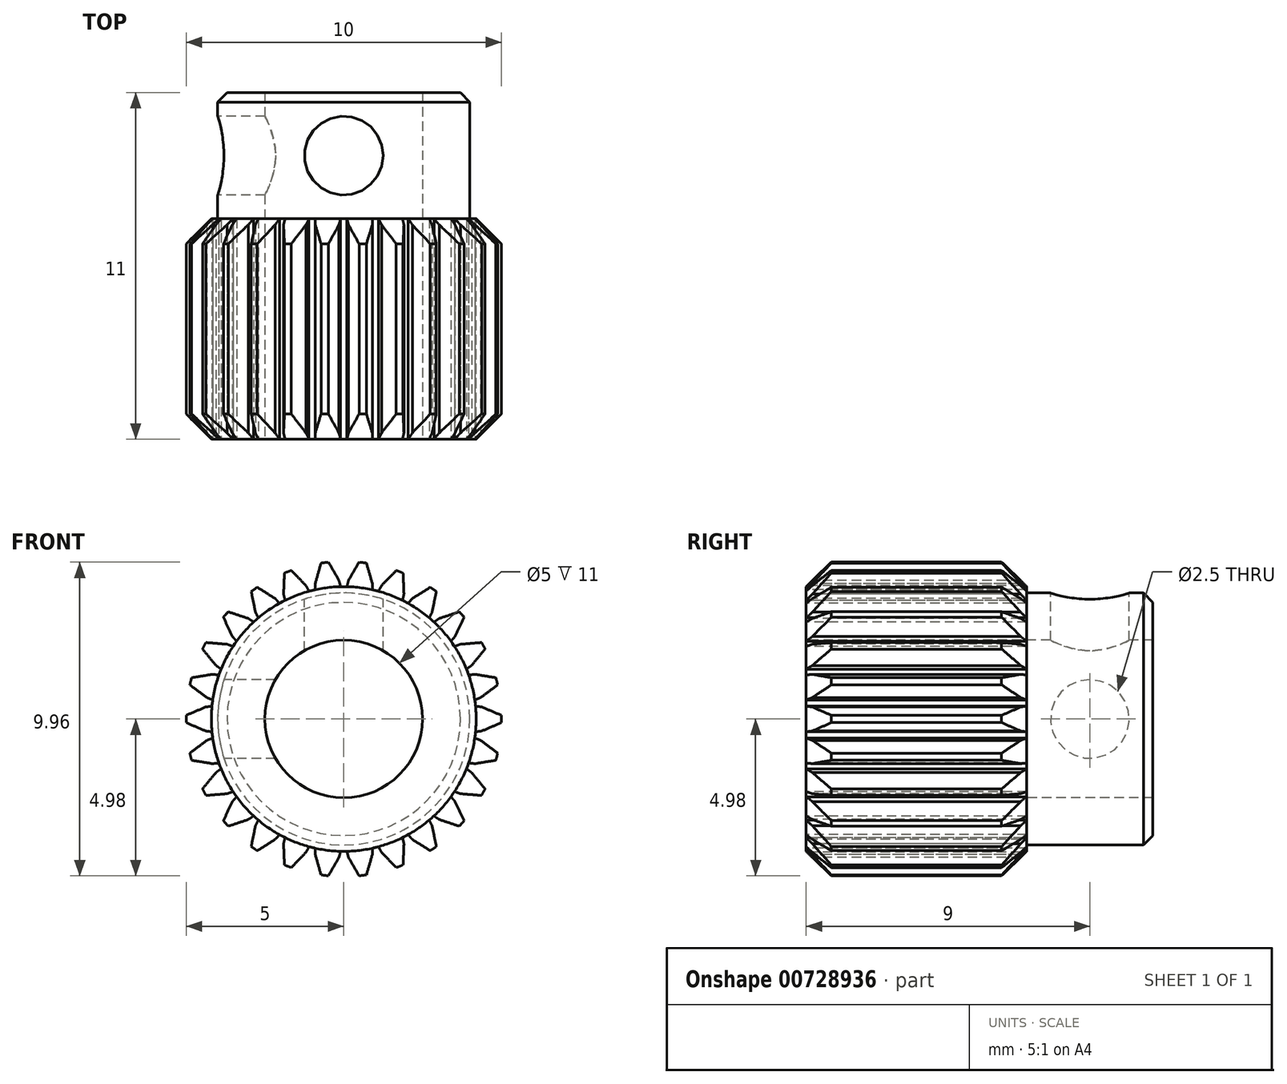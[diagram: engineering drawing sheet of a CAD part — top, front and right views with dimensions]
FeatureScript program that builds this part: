
annotation { "Feature Type Name" : "Feature", "Feature Type Description" : "" }
export const myFeature = defineFeature(function(context is Context, id is Id, definition is map)
    precondition{}
    {
        {
            var Q0;
            Q0=qCreatedBy(makeId("Right.planeOp"),FACE);
            var sketch = newSketch(context, id + "F0", { "sketchPlane" : qUnion([Q0])});
            skLineSegment(sketch, "E0", {"start": v(-5.5, 0) * mm, "end": v(5.5, 0) * mm, "construction": true});
            skLineSegment(sketch, "E1", {"start": v(-5.5, 2.5) * mm, "end": v(5.5, 2.5) * mm});
            skLineSegment(sketch, "E2", {"start": v(5.5, 2.5) * mm, "end": v(5.5, 4) * mm});
            skLineSegment(sketch, "E3", {"start": v(5.5, 4) * mm, "end": v(1.5, 4) * mm});
            skLineSegment(sketch, "E4", {"start": v(1.5, 4) * mm, "end": v(1.5, 5) * mm});
            skLineSegment(sketch, "E5", {"start": v(1.5, 5) * mm, "end": v(-5.5, 5) * mm});
            skLineSegment(sketch, "E6", {"start": v(-5.5, 5) * mm, "end": v(-5.5, 2.5) * mm});
            skSolve(sketch);
        }
        {
            var Q0;
            Q0=makeQuery(id+"F0.imprint","IMPRINT",FACE,{"disambiguationData":[TD([[makeQuery(id+"F0.imprint","IMPRINT",EDGE,{"derivedFrom":sQuery(id+"F0.wireOp",EDGE,"E1")}),1.0]])]});
            var Q1;
            Q1=sQuery(id+"F0.wireOp",EDGE,"E0");
            revolve(context, id + "F1", {"entities" : qUnion([Q0]), "axis" : qUnion([Q1]), "revolveType" : RevolveType.FULL});
        }
        {
            var Q0;
            Q0=makeQuery(id+"F1.opRevolve","SWEPT_EDGE",EDGE,{"disambiguationData":[OSD([sQuery(id+"F0.wireOp",EDGE,"E4"),sQuery(id+"F0.wireOp",EDGE,"E5")])]});
            var Q1;
            Q1=makeQuery(id+"F1.opRevolve","SWEPT_EDGE",EDGE,{"disambiguationData":[OSD([sQuery(id+"F0.wireOp",EDGE,"E5"),sQuery(id+"F0.wireOp",EDGE,"E6")])]});
            chamfer(context, id + "F2", {"entities" : qUnion([Q0, Q1]), "width" : .8 * mm, "tangentPropagation" : true});
        }
        {
            var Q0;
            Q0=makeQuery(id+"F1.opRevolve","SWEPT_FACE",FACE,{"disambiguationData":[OSD([sQuery(id+"F0.wireOp",EDGE,"E6")])]});
            var sketch = newSketch(context, id + "F3", { "sketchPlane" : qUnion([Q0])});
            skLineSegment(sketch, "E7", {"start": v(0, 0) * mm, "end": v(0, 5) * mm, "construction": true});
            skLineSegment(sketch, "E8", {"start": v(0, 4.2) * mm, "end": v(-0.1, 4.2) * mm});
            skLineSegment(sketch, "E9", {"start": v(-0.1, 4.2) * mm, "end": v(-0.15, 4.4) * mm});
            skLineSegment(sketch, "E10", {"start": v(-0.15, 4.4) * mm, "end": v(-0.5, 5) * mm});
            skLineSegment(sketch, "E11", {"start": v(0, 5) * mm, "end": v(-0.5, 5) * mm});
            skLineSegment(sketch, "E12.MirrorCS", {"start": v(0, 5) * mm, "end": v(0.5, 5) * mm});
            skLineSegment(sketch, "E13.MirrorCS", {"start": v(0.15, 4.4) * mm, "end": v(0.5, 5) * mm});
            skLineSegment(sketch, "E14.MirrorCS", {"start": v(0, 4.2) * mm, "end": v(0.1, 4.2) * mm});
            skLineSegment(sketch, "E15.MirrorCS", {"start": v(0.1, 4.2) * mm, "end": v(0.15, 4.4) * mm});
            skLineSegment(sketch, "E16.1.0", {"start": v(-0.9, 4.3) * mm, "end": v(-0.71, 4.97) * mm});
            skLineSegment(sketch, "E16.1.1", {"start": v(-1.2, 4.85) * mm, "end": v(-0.71, 4.97) * mm});
            skLineSegment(sketch, "E16.1.2", {"start": v(-1.2, 4.85) * mm, "end": v(-1.68, 4.74) * mm});
            skLineSegment(sketch, "E16.1.3", {"start": v(-1.2, 4.23) * mm, "end": v(-1.68, 4.74) * mm});
            skLineSegment(sketch, "E16.1.4", {"start": v(-1.1, 4.05) * mm, "end": v(-1.2, 4.23) * mm});
            skLineSegment(sketch, "E16.1.5", {"start": v(-0.9, 4.1) * mm, "end": v(-0.9, 4.3) * mm});
            skLineSegment(sketch, "E16.1.6", {"start": v(-1, 4.08) * mm, "end": v(-1.1, 4.05) * mm});
            skLineSegment(sketch, "E16.1.7", {"start": v(-1, 4.08) * mm, "end": v(-0.9, 4.1) * mm});
            skLineSegment(sketch, "E16.2.0", {"start": v(-1.9, 3.96) * mm, "end": v(-1.88, 4.66) * mm});
            skLineSegment(sketch, "E16.2.1", {"start": v(-2.32, 4.43) * mm, "end": v(-1.88, 4.66) * mm});
            skLineSegment(sketch, "E16.2.2", {"start": v(-2.32, 4.43) * mm, "end": v(-2.77, 4.2) * mm});
            skLineSegment(sketch, "E16.2.3", {"start": v(-2.17, 3.82) * mm, "end": v(-2.77, 4.2) * mm});
            skLineSegment(sketch, "E16.2.4", {"start": v(-2.04, 3.67) * mm, "end": v(-2.17, 3.82) * mm});
            skLineSegment(sketch, "E16.2.5", {"start": v(-1.86, 3.77) * mm, "end": v(-1.9, 3.96) * mm});
            skLineSegment(sketch, "E16.2.6", {"start": v(-1.95, 3.72) * mm, "end": v(-2.04, 3.67) * mm});
            skLineSegment(sketch, "E16.2.7", {"start": v(-1.95, 3.72) * mm, "end": v(-1.86, 3.77) * mm});
            skLineSegment(sketch, "E16.3.0", {"start": v(-2.8, 3.39) * mm, "end": v(-2.94, 4.07) * mm});
            skLineSegment(sketch, "E16.3.1", {"start": v(-3.32, 3.74) * mm, "end": v(-2.94, 4.07) * mm});
            skLineSegment(sketch, "E16.3.2", {"start": v(-3.32, 3.74) * mm, "end": v(-3.69, 3.41) * mm});
            skLineSegment(sketch, "E16.3.3", {"start": v(-3.03, 3.19) * mm, "end": v(-3.69, 3.41) * mm});
            skLineSegment(sketch, "E16.3.4", {"start": v(-2.86, 3.08) * mm, "end": v(-3.03, 3.19) * mm});
            skLineSegment(sketch, "E16.3.5", {"start": v(-2.71, 3.21) * mm, "end": v(-2.8, 3.39) * mm});
            skLineSegment(sketch, "E16.3.6", {"start": v(-2.79, 3.14) * mm, "end": v(-2.86, 3.08) * mm});
            skLineSegment(sketch, "E16.3.7", {"start": v(-2.79, 3.14) * mm, "end": v(-2.71, 3.21) * mm});
            skLineSegment(sketch, "E16.4.0", {"start": v(-3.53, 2.62) * mm, "end": v(-3.83, 3.25) * mm});
            skLineSegment(sketch, "E16.4.1", {"start": v(-4.11, 2.84) * mm, "end": v(-3.83, 3.25) * mm});
            skLineSegment(sketch, "E16.4.2", {"start": v(-4.11, 2.84) * mm, "end": v(-4.4, 2.43) * mm});
            skLineSegment(sketch, "E16.4.3", {"start": v(-3.7, 2.37) * mm, "end": v(-4.4, 2.43) * mm});
            skLineSegment(sketch, "E16.4.4", {"start": v(-3.51, 2.3) * mm, "end": v(-3.7, 2.37) * mm});
            skLineSegment(sketch, "E16.4.5", {"start": v(-3.4, 2.47) * mm, "end": v(-3.53, 2.62) * mm});
            skLineSegment(sketch, "E16.4.6", {"start": v(-3.46, 2.39) * mm, "end": v(-3.51, 2.3) * mm});
            skLineSegment(sketch, "E16.4.7", {"start": v(-3.46, 2.39) * mm, "end": v(-3.4, 2.47) * mm});
            skLineSegment(sketch, "E16.5.0", {"start": v(-4.06, 1.7) * mm, "end": v(-4.5, 2.24) * mm});
            skLineSegment(sketch, "E16.5.1", {"start": v(-4.68, 1.77) * mm, "end": v(-4.5, 2.24) * mm});
            skLineSegment(sketch, "E16.5.2", {"start": v(-4.68, 1.77) * mm, "end": v(-4.85, 1.3) * mm});
            skLineSegment(sketch, "E16.5.3", {"start": v(-4.16, 1.42) * mm, "end": v(-4.85, 1.3) * mm});
            skLineSegment(sketch, "E16.5.4", {"start": v(-3.96, 1.4) * mm, "end": v(-4.16, 1.42) * mm});
            skLineSegment(sketch, "E16.5.5", {"start": v(-3.9, 1.58) * mm, "end": v(-4.06, 1.7) * mm});
            skLineSegment(sketch, "E16.5.6", {"start": v(-3.93, 1.49) * mm, "end": v(-3.96, 1.4) * mm});
            skLineSegment(sketch, "E16.5.7", {"start": v(-3.93, 1.49) * mm, "end": v(-3.9, 1.58) * mm});
            skLineSegment(sketch, "E16.6.0", {"start": v(-4.34, 0.68) * mm, "end": v(-4.9, 1.1) * mm});
            skLineSegment(sketch, "E16.6.1", {"start": v(-4.96, 0.6) * mm, "end": v(-4.9, 1.1) * mm});
            skLineSegment(sketch, "E16.6.2", {"start": v(-4.96, 0.6) * mm, "end": v(-5.02, 0.1) * mm});
            skLineSegment(sketch, "E16.6.3", {"start": v(-4.38, 0.38) * mm, "end": v(-5.02, 0.1) * mm});
            skLineSegment(sketch, "E16.6.4", {"start": v(-4.18, 0.4) * mm, "end": v(-4.38, 0.38) * mm});
            skLineSegment(sketch, "E16.6.5", {"start": v(-4.16, 0.6) * mm, "end": v(-4.34, 0.68) * mm});
            skLineSegment(sketch, "E16.6.6", {"start": v(-4.17, 0.5) * mm, "end": v(-4.18, 0.4) * mm});
            skLineSegment(sketch, "E16.6.7", {"start": v(-4.17, 0.5) * mm, "end": v(-4.16, 0.6) * mm});
            skLineSegment(sketch, "E16.7.0", {"start": v(-4.38, -0.38) * mm, "end": v(-5.02, -0.1) * mm});
            skLineSegment(sketch, "E16.7.1", {"start": v(-4.96, -0.6) * mm, "end": v(-5.02, -0.1) * mm});
            skLineSegment(sketch, "E16.7.2", {"start": v(-4.96, -0.6) * mm, "end": v(-4.9, -1.1) * mm});
            skLineSegment(sketch, "E16.7.3", {"start": v(-4.34, -0.68) * mm, "end": v(-4.9, -1.1) * mm});
            skLineSegment(sketch, "E16.7.4", {"start": v(-4.16, -0.6) * mm, "end": v(-4.34, -0.68) * mm});
            skLineSegment(sketch, "E16.7.5", {"start": v(-4.18, -0.4) * mm, "end": v(-4.38, -0.38) * mm});
            skLineSegment(sketch, "E16.7.6", {"start": v(-4.17, -0.5) * mm, "end": v(-4.16, -0.6) * mm});
            skLineSegment(sketch, "E16.7.7", {"start": v(-4.17, -0.5) * mm, "end": v(-4.18, -0.4) * mm});
            skLineSegment(sketch, "E16.8.0", {"start": v(-4.16, -1.42) * mm, "end": v(-4.85, -1.3) * mm});
            skLineSegment(sketch, "E16.8.1", {"start": v(-4.68, -1.77) * mm, "end": v(-4.85, -1.3) * mm});
            skLineSegment(sketch, "E16.8.2", {"start": v(-4.68, -1.77) * mm, "end": v(-4.5, -2.24) * mm});
            skLineSegment(sketch, "E16.8.3", {"start": v(-4.06, -1.7) * mm, "end": v(-4.5, -2.24) * mm});
            skLineSegment(sketch, "E16.8.4", {"start": v(-3.9, -1.58) * mm, "end": v(-4.06, -1.7) * mm});
            skLineSegment(sketch, "E16.8.5", {"start": v(-3.96, -1.4) * mm, "end": v(-4.16, -1.42) * mm});
            skLineSegment(sketch, "E16.8.6", {"start": v(-3.93, -1.49) * mm, "end": v(-3.9, -1.58) * mm});
            skLineSegment(sketch, "E16.8.7", {"start": v(-3.93, -1.49) * mm, "end": v(-3.96, -1.4) * mm});
            skLineSegment(sketch, "E16.9.0", {"start": v(-3.7, -2.37) * mm, "end": v(-4.4, -2.43) * mm});
            skLineSegment(sketch, "E16.9.1", {"start": v(-4.11, -2.84) * mm, "end": v(-4.4, -2.43) * mm});
            skLineSegment(sketch, "E16.9.2", {"start": v(-4.11, -2.84) * mm, "end": v(-3.83, -3.25) * mm});
            skLineSegment(sketch, "E16.9.3", {"start": v(-3.53, -2.62) * mm, "end": v(-3.83, -3.25) * mm});
            skLineSegment(sketch, "E16.9.4", {"start": v(-3.4, -2.47) * mm, "end": v(-3.53, -2.62) * mm});
            skLineSegment(sketch, "E16.9.5", {"start": v(-3.51, -2.3) * mm, "end": v(-3.7, -2.37) * mm});
            skLineSegment(sketch, "E16.9.6", {"start": v(-3.46, -2.39) * mm, "end": v(-3.4, -2.47) * mm});
            skLineSegment(sketch, "E16.9.7", {"start": v(-3.46, -2.39) * mm, "end": v(-3.51, -2.3) * mm});
            skLineSegment(sketch, "E16.10.0", {"start": v(-3.03, -3.19) * mm, "end": v(-3.69, -3.41) * mm});
            skLineSegment(sketch, "E16.10.1", {"start": v(-3.32, -3.74) * mm, "end": v(-3.69, -3.41) * mm});
            skLineSegment(sketch, "E16.10.2", {"start": v(-3.32, -3.74) * mm, "end": v(-2.94, -4.07) * mm});
            skLineSegment(sketch, "E16.10.3", {"start": v(-2.8, -3.39) * mm, "end": v(-2.94, -4.07) * mm});
            skLineSegment(sketch, "E16.10.4", {"start": v(-2.71, -3.21) * mm, "end": v(-2.8, -3.39) * mm});
            skLineSegment(sketch, "E16.10.5", {"start": v(-2.86, -3.08) * mm, "end": v(-3.03, -3.19) * mm});
            skLineSegment(sketch, "E16.10.6", {"start": v(-2.79, -3.14) * mm, "end": v(-2.71, -3.21) * mm});
            skLineSegment(sketch, "E16.10.7", {"start": v(-2.79, -3.14) * mm, "end": v(-2.86, -3.08) * mm});
            skLineSegment(sketch, "E16.11.0", {"start": v(-2.17, -3.82) * mm, "end": v(-2.77, -4.2) * mm});
            skLineSegment(sketch, "E16.11.1", {"start": v(-2.32, -4.43) * mm, "end": v(-2.77, -4.2) * mm});
            skLineSegment(sketch, "E16.11.2", {"start": v(-2.32, -4.43) * mm, "end": v(-1.88, -4.66) * mm});
            skLineSegment(sketch, "E16.11.3", {"start": v(-1.9, -3.96) * mm, "end": v(-1.88, -4.66) * mm});
            skLineSegment(sketch, "E16.11.4", {"start": v(-1.86, -3.77) * mm, "end": v(-1.9, -3.96) * mm});
            skLineSegment(sketch, "E16.11.5", {"start": v(-2.04, -3.67) * mm, "end": v(-2.17, -3.82) * mm});
            skLineSegment(sketch, "E16.11.6", {"start": v(-1.95, -3.72) * mm, "end": v(-1.86, -3.77) * mm});
            skLineSegment(sketch, "E16.11.7", {"start": v(-1.95, -3.72) * mm, "end": v(-2.04, -3.67) * mm});
            skLineSegment(sketch, "E16.12.0", {"start": v(-1.2, -4.23) * mm, "end": v(-1.68, -4.74) * mm});
            skLineSegment(sketch, "E16.12.1", {"start": v(-1.2, -4.85) * mm, "end": v(-1.68, -4.74) * mm});
            skLineSegment(sketch, "E16.12.2", {"start": v(-1.2, -4.85) * mm, "end": v(-0.71, -4.97) * mm});
            skLineSegment(sketch, "E16.12.3", {"start": v(-0.9, -4.3) * mm, "end": v(-0.71, -4.97) * mm});
            skLineSegment(sketch, "E16.12.4", {"start": v(-0.9, -4.1) * mm, "end": v(-0.9, -4.3) * mm});
            skLineSegment(sketch, "E16.12.5", {"start": v(-1.1, -4.05) * mm, "end": v(-1.2, -4.23) * mm});
            skLineSegment(sketch, "E16.12.6", {"start": v(-1, -4.08) * mm, "end": v(-0.9, -4.1) * mm});
            skLineSegment(sketch, "E16.12.7", {"start": v(-1, -4.08) * mm, "end": v(-1.1, -4.05) * mm});
            skLineSegment(sketch, "E16.13.0", {"start": v(-0.15, -4.4) * mm, "end": v(-0.5, -5) * mm});
            skLineSegment(sketch, "E16.13.1", {"start": v(0, -5) * mm, "end": v(-0.5, -5) * mm});
            skLineSegment(sketch, "E16.13.2", {"start": v(0, -5) * mm, "end": v(0.5, -5) * mm});
            skLineSegment(sketch, "E16.13.3", {"start": v(0.15, -4.4) * mm, "end": v(0.5, -5) * mm});
            skLineSegment(sketch, "E16.13.4", {"start": v(0.1, -4.2) * mm, "end": v(0.15, -4.4) * mm});
            skLineSegment(sketch, "E16.13.5", {"start": v(-0.1, -4.2) * mm, "end": v(-0.15, -4.4) * mm});
            skLineSegment(sketch, "E16.13.6", {"start": v(0, -4.2) * mm, "end": v(0.1, -4.2) * mm});
            skLineSegment(sketch, "E16.13.7", {"start": v(0, -4.2) * mm, "end": v(-0.1, -4.2) * mm});
            skLineSegment(sketch, "E16.14.0", {"start": v(0.9, -4.3) * mm, "end": v(0.71, -4.97) * mm});
            skLineSegment(sketch, "E16.14.1", {"start": v(1.2, -4.85) * mm, "end": v(0.71, -4.97) * mm});
            skLineSegment(sketch, "E16.14.2", {"start": v(1.2, -4.85) * mm, "end": v(1.68, -4.74) * mm});
            skLineSegment(sketch, "E16.14.3", {"start": v(1.2, -4.23) * mm, "end": v(1.68, -4.74) * mm});
            skLineSegment(sketch, "E16.14.4", {"start": v(1.1, -4.05) * mm, "end": v(1.2, -4.23) * mm});
            skLineSegment(sketch, "E16.14.5", {"start": v(0.9, -4.1) * mm, "end": v(0.9, -4.3) * mm});
            skLineSegment(sketch, "E16.14.6", {"start": v(1, -4.08) * mm, "end": v(1.1, -4.05) * mm});
            skLineSegment(sketch, "E16.14.7", {"start": v(1, -4.08) * mm, "end": v(0.9, -4.1) * mm});
            skLineSegment(sketch, "E16.15.0", {"start": v(1.9, -3.96) * mm, "end": v(1.88, -4.66) * mm});
            skLineSegment(sketch, "E16.15.1", {"start": v(2.32, -4.43) * mm, "end": v(1.88, -4.66) * mm});
            skLineSegment(sketch, "E16.15.2", {"start": v(2.32, -4.43) * mm, "end": v(2.77, -4.2) * mm});
            skLineSegment(sketch, "E16.15.3", {"start": v(2.17, -3.82) * mm, "end": v(2.77, -4.2) * mm});
            skLineSegment(sketch, "E16.15.4", {"start": v(2.04, -3.67) * mm, "end": v(2.17, -3.82) * mm});
            skLineSegment(sketch, "E16.15.5", {"start": v(1.86, -3.77) * mm, "end": v(1.9, -3.96) * mm});
            skLineSegment(sketch, "E16.15.6", {"start": v(1.95, -3.72) * mm, "end": v(2.04, -3.67) * mm});
            skLineSegment(sketch, "E16.15.7", {"start": v(1.95, -3.72) * mm, "end": v(1.86, -3.77) * mm});
            skLineSegment(sketch, "E16.16.0", {"start": v(2.8, -3.39) * mm, "end": v(2.94, -4.07) * mm});
            skLineSegment(sketch, "E16.16.1", {"start": v(3.32, -3.74) * mm, "end": v(2.94, -4.07) * mm});
            skLineSegment(sketch, "E16.16.2", {"start": v(3.32, -3.74) * mm, "end": v(3.69, -3.41) * mm});
            skLineSegment(sketch, "E16.16.3", {"start": v(3.03, -3.19) * mm, "end": v(3.69, -3.41) * mm});
            skLineSegment(sketch, "E16.16.4", {"start": v(2.86, -3.08) * mm, "end": v(3.03, -3.19) * mm});
            skLineSegment(sketch, "E16.16.5", {"start": v(2.71, -3.21) * mm, "end": v(2.8, -3.39) * mm});
            skLineSegment(sketch, "E16.16.6", {"start": v(2.79, -3.14) * mm, "end": v(2.86, -3.08) * mm});
            skLineSegment(sketch, "E16.16.7", {"start": v(2.79, -3.14) * mm, "end": v(2.71, -3.21) * mm});
            skLineSegment(sketch, "E16.17.0", {"start": v(3.53, -2.62) * mm, "end": v(3.83, -3.25) * mm});
            skLineSegment(sketch, "E16.17.1", {"start": v(4.11, -2.84) * mm, "end": v(3.83, -3.25) * mm});
            skLineSegment(sketch, "E16.17.2", {"start": v(4.11, -2.84) * mm, "end": v(4.4, -2.43) * mm});
            skLineSegment(sketch, "E16.17.3", {"start": v(3.7, -2.37) * mm, "end": v(4.4, -2.43) * mm});
            skLineSegment(sketch, "E16.17.4", {"start": v(3.51, -2.3) * mm, "end": v(3.7, -2.37) * mm});
            skLineSegment(sketch, "E16.17.5", {"start": v(3.4, -2.47) * mm, "end": v(3.53, -2.62) * mm});
            skLineSegment(sketch, "E16.17.6", {"start": v(3.46, -2.39) * mm, "end": v(3.51, -2.3) * mm});
            skLineSegment(sketch, "E16.17.7", {"start": v(3.46, -2.39) * mm, "end": v(3.4, -2.47) * mm});
            skLineSegment(sketch, "E16.18.0", {"start": v(4.06, -1.7) * mm, "end": v(4.5, -2.24) * mm});
            skLineSegment(sketch, "E16.18.1", {"start": v(4.68, -1.77) * mm, "end": v(4.5, -2.24) * mm});
            skLineSegment(sketch, "E16.18.2", {"start": v(4.68, -1.77) * mm, "end": v(4.85, -1.3) * mm});
            skLineSegment(sketch, "E16.18.3", {"start": v(4.16, -1.42) * mm, "end": v(4.85, -1.3) * mm});
            skLineSegment(sketch, "E16.18.4", {"start": v(3.96, -1.4) * mm, "end": v(4.16, -1.42) * mm});
            skLineSegment(sketch, "E16.18.5", {"start": v(3.9, -1.58) * mm, "end": v(4.06, -1.7) * mm});
            skLineSegment(sketch, "E16.18.6", {"start": v(3.93, -1.49) * mm, "end": v(3.96, -1.4) * mm});
            skLineSegment(sketch, "E16.18.7", {"start": v(3.93, -1.49) * mm, "end": v(3.9, -1.58) * mm});
            skLineSegment(sketch, "E16.19.0", {"start": v(4.34, -0.68) * mm, "end": v(4.9, -1.1) * mm});
            skLineSegment(sketch, "E16.19.1", {"start": v(4.96, -0.6) * mm, "end": v(4.9, -1.1) * mm});
            skLineSegment(sketch, "E16.19.2", {"start": v(4.96, -0.6) * mm, "end": v(5.02, -0.1) * mm});
            skLineSegment(sketch, "E16.19.3", {"start": v(4.38, -0.38) * mm, "end": v(5.02, -0.1) * mm});
            skLineSegment(sketch, "E16.19.4", {"start": v(4.18, -0.4) * mm, "end": v(4.38, -0.38) * mm});
            skLineSegment(sketch, "E16.19.5", {"start": v(4.16, -0.6) * mm, "end": v(4.34, -0.68) * mm});
            skLineSegment(sketch, "E16.19.6", {"start": v(4.17, -0.5) * mm, "end": v(4.18, -0.4) * mm});
            skLineSegment(sketch, "E16.19.7", {"start": v(4.17, -0.5) * mm, "end": v(4.16, -0.6) * mm});
            skLineSegment(sketch, "E16.20.0", {"start": v(4.38, 0.38) * mm, "end": v(5.02, 0.1) * mm});
            skLineSegment(sketch, "E16.20.1", {"start": v(4.96, 0.6) * mm, "end": v(5.02, 0.1) * mm});
            skLineSegment(sketch, "E16.20.2", {"start": v(4.96, 0.6) * mm, "end": v(4.9, 1.1) * mm});
            skLineSegment(sketch, "E16.20.3", {"start": v(4.34, 0.68) * mm, "end": v(4.9, 1.1) * mm});
            skLineSegment(sketch, "E16.20.4", {"start": v(4.16, 0.6) * mm, "end": v(4.34, 0.68) * mm});
            skLineSegment(sketch, "E16.20.5", {"start": v(4.18, 0.4) * mm, "end": v(4.38, 0.38) * mm});
            skLineSegment(sketch, "E16.20.6", {"start": v(4.17, 0.5) * mm, "end": v(4.16, 0.6) * mm});
            skLineSegment(sketch, "E16.20.7", {"start": v(4.17, 0.5) * mm, "end": v(4.18, 0.4) * mm});
            skLineSegment(sketch, "E16.21.0", {"start": v(4.16, 1.42) * mm, "end": v(4.85, 1.3) * mm});
            skLineSegment(sketch, "E16.21.1", {"start": v(4.68, 1.77) * mm, "end": v(4.85, 1.3) * mm});
            skLineSegment(sketch, "E16.21.2", {"start": v(4.68, 1.77) * mm, "end": v(4.5, 2.24) * mm});
            skLineSegment(sketch, "E16.21.3", {"start": v(4.06, 1.7) * mm, "end": v(4.5, 2.24) * mm});
            skLineSegment(sketch, "E16.21.4", {"start": v(3.9, 1.58) * mm, "end": v(4.06, 1.7) * mm});
            skLineSegment(sketch, "E16.21.5", {"start": v(3.96, 1.4) * mm, "end": v(4.16, 1.42) * mm});
            skLineSegment(sketch, "E16.21.6", {"start": v(3.93, 1.49) * mm, "end": v(3.9, 1.58) * mm});
            skLineSegment(sketch, "E16.21.7", {"start": v(3.93, 1.49) * mm, "end": v(3.96, 1.4) * mm});
            skLineSegment(sketch, "E16.22.0", {"start": v(3.7, 2.37) * mm, "end": v(4.4, 2.43) * mm});
            skLineSegment(sketch, "E16.22.1", {"start": v(4.11, 2.84) * mm, "end": v(4.4, 2.43) * mm});
            skLineSegment(sketch, "E16.22.2", {"start": v(4.11, 2.84) * mm, "end": v(3.83, 3.25) * mm});
            skLineSegment(sketch, "E16.22.3", {"start": v(3.53, 2.62) * mm, "end": v(3.83, 3.25) * mm});
            skLineSegment(sketch, "E16.22.4", {"start": v(3.4, 2.47) * mm, "end": v(3.53, 2.62) * mm});
            skLineSegment(sketch, "E16.22.5", {"start": v(3.51, 2.3) * mm, "end": v(3.7, 2.37) * mm});
            skLineSegment(sketch, "E16.22.6", {"start": v(3.46, 2.39) * mm, "end": v(3.4, 2.47) * mm});
            skLineSegment(sketch, "E16.22.7", {"start": v(3.46, 2.39) * mm, "end": v(3.51, 2.3) * mm});
            skLineSegment(sketch, "E16.23.0", {"start": v(3.03, 3.19) * mm, "end": v(3.69, 3.41) * mm});
            skLineSegment(sketch, "E16.23.1", {"start": v(3.32, 3.74) * mm, "end": v(3.69, 3.41) * mm});
            skLineSegment(sketch, "E16.23.2", {"start": v(3.32, 3.74) * mm, "end": v(2.94, 4.07) * mm});
            skLineSegment(sketch, "E16.23.3", {"start": v(2.8, 3.39) * mm, "end": v(2.94, 4.07) * mm});
            skLineSegment(sketch, "E16.23.4", {"start": v(2.71, 3.21) * mm, "end": v(2.8, 3.39) * mm});
            skLineSegment(sketch, "E16.23.5", {"start": v(2.86, 3.08) * mm, "end": v(3.03, 3.19) * mm});
            skLineSegment(sketch, "E16.23.6", {"start": v(2.79, 3.14) * mm, "end": v(2.71, 3.21) * mm});
            skLineSegment(sketch, "E16.23.7", {"start": v(2.79, 3.14) * mm, "end": v(2.86, 3.08) * mm});
            skLineSegment(sketch, "E16.24.0", {"start": v(2.17, 3.82) * mm, "end": v(2.77, 4.2) * mm});
            skLineSegment(sketch, "E16.24.1", {"start": v(2.32, 4.43) * mm, "end": v(2.77, 4.2) * mm});
            skLineSegment(sketch, "E16.24.2", {"start": v(2.32, 4.43) * mm, "end": v(1.88, 4.66) * mm});
            skLineSegment(sketch, "E16.24.3", {"start": v(1.9, 3.96) * mm, "end": v(1.88, 4.66) * mm});
            skLineSegment(sketch, "E16.24.4", {"start": v(1.86, 3.77) * mm, "end": v(1.9, 3.96) * mm});
            skLineSegment(sketch, "E16.24.5", {"start": v(2.04, 3.67) * mm, "end": v(2.17, 3.82) * mm});
            skLineSegment(sketch, "E16.24.6", {"start": v(1.95, 3.72) * mm, "end": v(1.86, 3.77) * mm});
            skLineSegment(sketch, "E16.24.7", {"start": v(1.95, 3.72) * mm, "end": v(2.04, 3.67) * mm});
            skLineSegment(sketch, "E16.25.0", {"start": v(1.2, 4.23) * mm, "end": v(1.68, 4.74) * mm});
            skLineSegment(sketch, "E16.25.1", {"start": v(1.2, 4.85) * mm, "end": v(1.68, 4.74) * mm});
            skLineSegment(sketch, "E16.25.2", {"start": v(1.2, 4.85) * mm, "end": v(0.71, 4.97) * mm});
            skLineSegment(sketch, "E16.25.3", {"start": v(0.9, 4.3) * mm, "end": v(0.71, 4.97) * mm});
            skLineSegment(sketch, "E16.25.4", {"start": v(0.9, 4.1) * mm, "end": v(0.9, 4.3) * mm});
            skLineSegment(sketch, "E16.25.5", {"start": v(1.1, 4.05) * mm, "end": v(1.2, 4.23) * mm});
            skLineSegment(sketch, "E16.25.6", {"start": v(1, 4.08) * mm, "end": v(0.9, 4.1) * mm});
            skLineSegment(sketch, "E16.25.7", {"start": v(1, 4.08) * mm, "end": v(1.1, 4.05) * mm});
            skPoint(sketch, "E16.center", {"position": v(0, 0) * mm});
            skSolve(sketch);
        }
        {
            var Q0;
            Q0=qSketchRegion(id+"F3",true);
            extrude(context, id + "F4", {"entities" : qUnion([Q0]), "operationType" : NewBodyOperationType.REMOVE, "oppositeDirection" : true, "depth" : 10 * mm});
        }
        {
            var Q0;
            Q0=makeQuery(id+"F1.opRevolve","SWEPT_FACE",FACE,{"disambiguationData":[OSD([sQuery(id+"F0.wireOp",EDGE,"E2")])]});
            cPlane(context, id + "F5", {"entities" : qUnion([Q0]), "cplaneType" : CPlaneType.OFFSET, "offset" : 2 * mm, "oppositeDirection" : true, "width" : 150 * mm, "height" : 150 * mm});
        }
        {
            var Q0;
            Q0=qCreatedBy(id+"F5.planeOp",FACE);
            var sketch = newSketch(context, id + "F6", { "sketchPlane" : qUnion([Q0])});
            skLineSegment(sketch, "E17", {"start": v(0, 4) * mm, "end": v(0, 0) * mm});
            skLineSegment(sketch, "E18", {"start": v(0, 0) * mm, "end": v(4, 0) * mm});
            skSolve(sketch);
        }
        {
            var Q0;
            Q0=sQuery(id+"F6.wireOp",VERTEX,"E17.start");
            var Q1;
            Q1=sQuery(id+"F6.wireOp",EDGE,"E17");
            cPlane(context, id + "F7", {"entities" : qUnion([Q0, Q1]), "cplaneType" : CPlaneType.LINE_POINT, "offset" : 25 * mm, "width" : 150 * mm, "height" : 150 * mm});
        }
        {
            var Q0;
            Q0=qCreatedBy(id+"F7.planeOp",FACE);
            var sketch = newSketch(context, id + "F8", { "sketchPlane" : qUnion([Q0])});
            skPoint(sketch, "E19.0", {"position": v(0, -3.5) * mm});
            skSolve(sketch);
        }
        {
            var Q0;
            Q0=sQuery(id+"F6.wireOp",VERTEX,"E18.end");
            var Q1;
            Q1=sQuery(id+"F6.wireOp",EDGE,"E18");
            cPlane(context, id + "F9", {"entities" : qUnion([Q0, Q1]), "cplaneType" : CPlaneType.LINE_POINT, "offset" : 25 * mm, "width" : 150 * mm, "height" : 150 * mm});
        }
        {
            var Q0;
            Q0=qCreatedBy(id+"F9.planeOp",FACE);
            var sketch = newSketch(context, id + "F10", { "sketchPlane" : qUnion([Q0])});
            skPoint(sketch, "E20.0", {"position": v(-3.5, 0) * mm});
            skSolve(sketch);
        }
        {
            var Q0;
            Q0=sQuery(id+"F8.wireOp",VERTEX,"E19.0");
            var Q1;
            Q1=makeQuery(id+"F1.opRevolve","SWEPT_BODY",BODY,{"disambiguationData":[OSD([sQuery(id+"F0.wireOp",EDGE,"E1"),sQuery(id+"F0.wireOp",EDGE,"E2"),sQuery(id+"F0.wireOp",EDGE,"E3"),sQuery(id+"F0.wireOp",EDGE,"E4"),sQuery(id+"F0.wireOp",EDGE,"E5"),sQuery(id+"F0.wireOp",EDGE,"E6")])]});
            hole(context, id + "F11", {"style" : HoleStyle.SIMPLE, "endStyle" : HoleEndStyle.BLIND, "oppositeDirection" : true, "holeDiameter" : 2.5 * mm, "holeDepth" : 4 * mm, "locations" : qUnion([Q0]), "scope" : qUnion([Q1])});
        }
        {
            var Q0;
            Q0=sQuery(id+"F10.wireOp",VERTEX,"E20.0");
            var Q1;
            Q1=makeQuery(id+"F1.opRevolve","SWEPT_BODY",BODY,{"disambiguationData":[OSD([sQuery(id+"F0.wireOp",EDGE,"E1"),sQuery(id+"F0.wireOp",EDGE,"E2"),sQuery(id+"F0.wireOp",EDGE,"E3"),sQuery(id+"F0.wireOp",EDGE,"E4"),sQuery(id+"F0.wireOp",EDGE,"E5"),sQuery(id+"F0.wireOp",EDGE,"E6")])]});
            hole(context, id + "F12", {"style" : HoleStyle.SIMPLE, "endStyle" : HoleEndStyle.BLIND, "holeDiameter" : 2.5 * mm, "holeDepth" : 4 * mm, "locations" : qUnion([Q0]), "scope" : qUnion([Q1])});
        }
        {
            var Q0;
            Q0=makeQuery(id+"F1.opRevolve","SWEPT_EDGE",EDGE,{"disambiguationData":[OSD([sQuery(id+"F0.wireOp",EDGE,"E2"),sQuery(id+"F0.wireOp",EDGE,"E3")])]});
            chamfer(context, id + "F13", {"entities" : qUnion([Q0]), "width" : .3 * mm, "tangentPropagation" : true});
        }
    });
